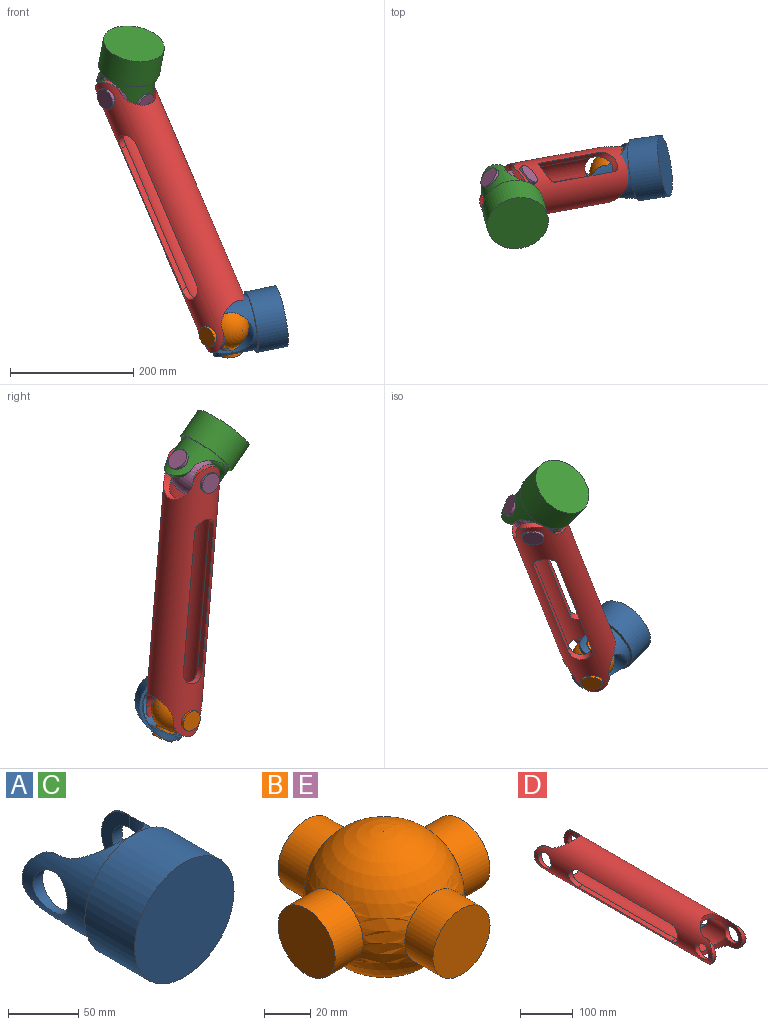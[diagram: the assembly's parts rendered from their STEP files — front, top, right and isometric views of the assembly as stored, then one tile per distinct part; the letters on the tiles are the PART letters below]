
ASSEMBLY  parts=5 mates=4
PART A: 11 faces, bbox 100x118.3x100 mm
  f0: cylinder r=45mm len=90mm, axis (0,-1,0), area 7768.4mm2, adj f4,f6,f7,f8,f9,f10
  f1: plane 56.57x28.28mm, normal (-1,0,0), area 775.6mm2, adj f6,f9,f10
  f2: plane 56.57x28.28mm, normal (1,0,0), area 775.6mm2, adj f6,f7,f8
  f3: cylinder r=50mm len=100mm, axis (0,-1,0), area 15708mm2, adj f4,f5
  f4: plane 100x100mm, normal (0,1,0), area 1492.3mm2, adj f0,f3
  f5: plane 100x100mm, normal (0,-1,0), area 7854mm2, adj f3
  f6: cylinder r=35mm len=90mm, axis (0,0,1), area 7167.4mm2, adj f0,f1,f2,f8,f10
  f7: cylinder r=28.28mm len=56.57mm, axis (1,0,0), area 458.2mm2, adj f0,f2
  f8: cylinder r=17.5mm len=35mm, axis (1,0,0), area 1033.1mm2, adj f0,f2,f6
  f9: cylinder r=28.28mm len=56.57mm, axis (1,0,0), area 458.1mm2, adj f0,f1
  f10: cylinder r=17.5mm len=35mm, axis (1,0,0), area 1033.8mm2, adj f0,f1,f6
PART B: 9 faces, bbox 95x95x70 mm
  f0: sphere r=35mm, area 11269mm2, adj f1,f4,f6,f7
  f1: cylinder r=17.5mm len=35mm, axis (0,1,0), area 1890mm2, adj f0,f2
  f2: plane 35x35mm, normal (0,1,0), area 962.1mm2, adj f1
  f3: plane 35x35mm, normal (0,-1,0), area 962.1mm2, adj f4
  f4: cylinder r=17.5mm len=35mm, axis (0,1,0), area 1890mm2, adj f0,f3
  f5: plane 35x35mm, normal (1,0,0), area 962.1mm2, adj f6
  f6: cylinder r=17.5mm len=35mm, axis (-1,0,0), area 1890mm2, adj f0,f5
  f7: cylinder r=17.5mm len=35mm, axis (-1,0,0), area 1890mm2, adj f0,f8
  f8: plane 35x35mm, normal (-1,0,0), area 962.1mm2, adj f7
PART C: same geometry as A
PART D: 26 faces, bbox 90x476.6x90 mm
  f0: cylinder r=45mm len=476.57mm, axis (0,1,0), area 88359.1mm2, adj f2,f3,f6,f7,f8,f9,f10,f11
  f1: cylinder r=35mm len=395.25mm, axis (0,1,0), area 57669.8mm2, adj f2,f3,f6,f7,f8,f9,f10,f11
  f2: cylinder r=35mm len=70mm, axis (0,0,1), area 1388.1mm2, adj f0,f1,f20,f21,f22,f23
  f3: cylinder r=35mm len=70mm, axis (0,0,1), area 1388.1mm2, adj f0,f1,f20,f21,f22,f23
  f4: plane 56.57x28.28mm, normal (-1,0,0), area 775.6mm2, adj f14,f15,f17,f19
  f5: plane 56.57x28.28mm, normal (1,0,0), area 775.6mm2, adj f14,f15,f16,f18
  f6: plane 250x11.59mm, normal (0,0,1), area 2897.1mm2, adj f0,f1,f7,f9
  f7: cylinder r=20mm len=40mm, axis (-1,0,0), area 675.4mm2, adj f0,f1,f6,f8
  f8: plane 250x11.59mm, normal (0,0,-1), area 2897.1mm2, adj f0,f1,f7,f9
  f9: cylinder r=20mm len=40mm, axis (-1,0,0), area 675.4mm2, adj f0,f1,f6,f8
  f10: cylinder r=20mm len=40mm, axis (-1,0,0), area 675.4mm2, adj f0,f1,f11,f13
  f11: plane 250x11.59mm, normal (0,0,-1), area 2897.1mm2, adj f0,f1,f10,f12
  f12: cylinder r=20mm len=40mm, axis (-1,0,0), area 675.4mm2, adj f0,f1,f11,f13
  f13: plane 250x11.59mm, normal (0,0,1), area 2897.1mm2, adj f0,f1,f10,f12
  f14: cylinder r=35mm len=70mm, axis (0,0,1), area 1388.1mm2, adj f0,f1,f4,f5,f16,f17
  f15: cylinder r=35mm len=70mm, axis (0,0,1), area 1388.1mm2, adj f0,f1,f4,f5,f16,f17
  f16: cylinder r=17.5mm len=35mm, axis (1,0,0), area 951.1mm2, adj f0,f1,f5,f14,f15
  f17: cylinder r=17.5mm len=35mm, axis (1,0,0), area 951.9mm2, adj f0,f1,f4,f14,f15
  f18: cylinder r=28.28mm len=56.57mm, axis (1,0,0), area 458.2mm2, adj f0,f5
  f19: cylinder r=28.28mm len=56.57mm, axis (1,0,0), area 458.1mm2, adj f0,f4
  f20: plane 56.57x28.28mm, normal (-1,0,0), area 775.6mm2, adj f2,f3,f23,f25
  f21: plane 56.57x28.28mm, normal (1,0,0), area 775.6mm2, adj f2,f3,f22,f24
  f22: cylinder r=17.5mm len=35mm, axis (1,0,0), area 951.9mm2, adj f0,f1,f2,f3,f21
  f23: cylinder r=17.5mm len=35mm, axis (1,0,0), area 951.1mm2, adj f0,f1,f2,f3,f20
  f24: cylinder r=28.28mm len=56.57mm, axis (1,0,0), area 458.1mm2, adj f0,f21
  f25: cylinder r=28.28mm len=56.57mm, axis (1,0,0), area 458.2mm2, adj f0,f20
PART E: same geometry as B
PLACE A rot(axis=(-0.59,0.38,0.71),109.7deg) t=(-279.6,-26.07,-274.82)mm
PLACE B rot(axis=(-0.81,-0.53,0.25),83deg) t=(-367,-38.89,-292.04)mm
PLACE C rot(axis=(-0.12,-0.86,0.49),137.1deg) t=(-518.09,-119.98,166.32)mm fixed
PLACE D rot(axis=(0.85,0.13,0.51),95.2deg) t=(-547.68,-72.63,129.65)mm
PLACE E rot(axis=(-0.91,-0.4,-0.07),144.1deg) t=(-531.97,-69.7,92.98)mm
MATE revolute B.f1 <-> A.f7  axis (0.13,0.37,-0.92) through (-371.45,-51.83,-259.82)mm
MATE revolute B.f6 <-> D.f22  axis (-0.7,-0.63,-0.35) through (-342.65,-16.91,-279.85)mm
MATE revolute C.f7 <-> E.f1  axis (0.71,-0.51,-0.49) through (-556.72,-51.72,109.98)mm
MATE revolute D.f16 <-> E.f6  axis (0.7,0.63,0.35) through (-556.31,-91.69,80.79)mm
